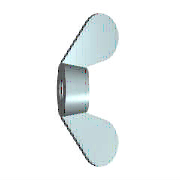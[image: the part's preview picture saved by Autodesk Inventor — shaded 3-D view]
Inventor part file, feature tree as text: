
AUTODESK INVENTOR PART (.ipt)
format: ipt  version: 2020 (Build 240168000, 168)  size: 171,008 bytes
history: native  units: mm (DEFAULTED — no unit token found)
features: sketch x2, extrude x1, mirror x1, hole x1, other x1, plane x1
ambient origin geometry x7: Origin, YZ Plane, XZ Plane, X Axis, Y Axis, Z Axis, Center Point
bodies: Solid1 (feature_tree), Body (feature_tree)
feature tree (7):
  sketch  "Sketch1"  dims[d0=7.0mm d1=7.5mm]
  extrude  "Wing1"  Depth=7.5mm
  mirror  "Wing2"
  hole  "Thread"  [1 undecoded]
  other  "Work Axis1"
  plane  "Work Plane1"
  sketch  "Sketch2"  dims[d2=7.0mm d3=3.0mm d57=90.0deg d4=4.6mm d5=8.0mm d6=1.9mm d7=0.0mm d8=0.633333mm d97=3.242mm d98=6.0mm d99=4.0mm d100=2.0mm d101=14.3117mm d102=8.0mm d103=20.594885mm d9=0.378886mm d10=30.0deg d11=0.0mm d108=0.0mm d109=0.378886mm d110=0.0mm d111=0.0mm d112=0.0mm]
note: 1 required parameter value undecoded (feature->parameter linkage not recoverable at this tier; creation-order binding heuristic only, values carry confidence <= 0.55)
